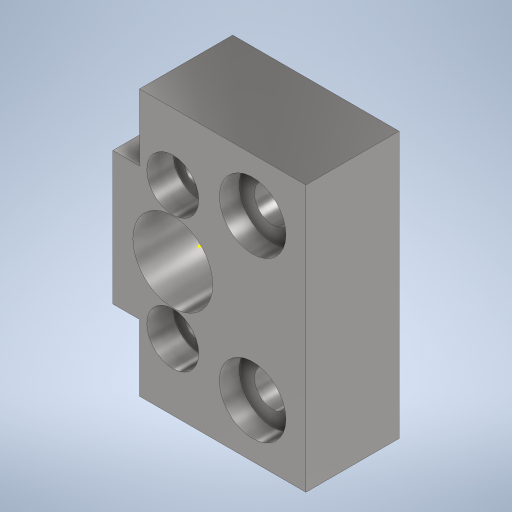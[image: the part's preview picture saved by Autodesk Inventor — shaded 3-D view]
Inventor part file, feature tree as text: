
AUTODESK INVENTOR PART (.ipt)
format: ipt  version: 2023 (Build 270158000, 158)  size: 370,176 bytes
history: native  units: mm
features: sketch x10, extrude x9, projected_geometry x4
ambient origin geometry x8: Origin, YZ Plane, XZ Plane, XY Plane, X Axis, Y Axis, Z Axis, Center Point
bodies: Solid1 (feature_tree)
feature tree (23):
  extrude  "Extrusion1"  Depth=10.0mm
  extrude  "Extrusion2"  Depth=10.0mm
  extrude  "Extrusion6"  Depth=5.0mm
  extrude  "Extrusion7"  Depth=2.4mm
  extrude  "Extrusion8"  Depth=5.0mm TaperAngle=0.0deg
  extrude  "Extrusion9"  Depth=4.0mm
  extrude  "Extrusion11"  Depth=4.0mm
  sketch  "Sketch13"  dims[d37=4.0mm d38=5.0mm]
  extrude  "Extrusion12"  Depth=5.0mm
  extrude  "Extrusion13"  Depth=5.0mm
  sketch  "Sketch1"  dims[d0=10.0mm d1=10.0mm]
  sketch  "Sketch2"  dims[d2=10.0mm d3=10.0mm]
  sketch  "Sketch7"  dims[d4=5.0mm d5=5.0mm]
  sketch  "Sketch8"  dims[d6=2.4mm d7=2.4mm]
  sketch  "Sketch9"  dims[d8=6.0mm d9=5.0mm d10=0.0mm]
  sketch  "Sketch10"  dims[d17=1.0mm d18=0.0mm d34=4.0mm]
  sketch  "Sketch12"  dims[d35=4.0mm d36=4.0mm]
  projected_geometry  "Projected Loop1"
  projected_geometry  "Projected Loop2"
  sketch  "Sketch14"  dims[d39=5.0mm d40=2.75mm]
  projected_geometry  "Projected Loop3"
  sketch  "Sketch15"  dims[d41=2.75mm d42=5.0mm d43=0.0mm d44=7.5mm d45=7.5mm d46=7.5mm d47=7.5mm d48=5.0mm d49=2.0mm d50=0.0mm d51=5.0mm d52=5.0mm d53=2.5mm d54=0.0mm d55=5.0mm d56=2.5mm d57=5.0mm d58=5.0mm d59=2.5mm d60=10.0mm d61=0.0mm d74=1.5mm d75=0.0mm d76=2.0mm d77=0.0mm d78=0.5mm d79=0.0mm d80=3.9mm d81=3.9mm d82=0.5mm d83=0.872665mm d84=0.5mm d85=0.872665mm]
  projected_geometry  "Projected Loop4"
